# Revit family: Furniture-Vanity-KOHLER-Jacquard-K-99564
name_source: partatom
category: Casework
units: mm (PartAtom-declared; Revit-internal decimal feet)

## family parameters
Cut with Voids When Loaded = No
Host = Face
OmniClass Number = 23.40.35.17.47.14
OmniClass Title = Bathroom Casework
Room Calculation Point = No
Shared = No

## types (1)
- Not a Type-See Type Catalog
    99564_LG = No
    99564_TK = No
    ADA Compliant = No
    Assembly Code = E2010
    Construction Type = Floor Mount
    Date Modified = 05/24/2018
    Default Elevation = 0"
    Depth = 21 7/8"
    Edition number = 1
    Hardware Included = No
    Height = 34 1/2"
    Manufacturer = KOHLER Co.
    MasterFormat 1995 = 08715
    MasterFormat 2004 = 08.71.73
    Material = Solid Wood and Veneers
    Product Documentation Link = http://www.us.kohler.com
    Product Finish = Default
    Product Guid = 643c9923-bdbf-41aa-a50f-473c72ef4e25
    Product Name = Jacquard
    Product Page URL = http://www.us.kohler.com
    Product data url = https://bimobject.com
    Type = 0
    URL = https://www.us.kohler.com
    Width = 42"

## geometry (parser evidence)
native form markers: Sweep x4
no freeform markers — native parametric forms only
